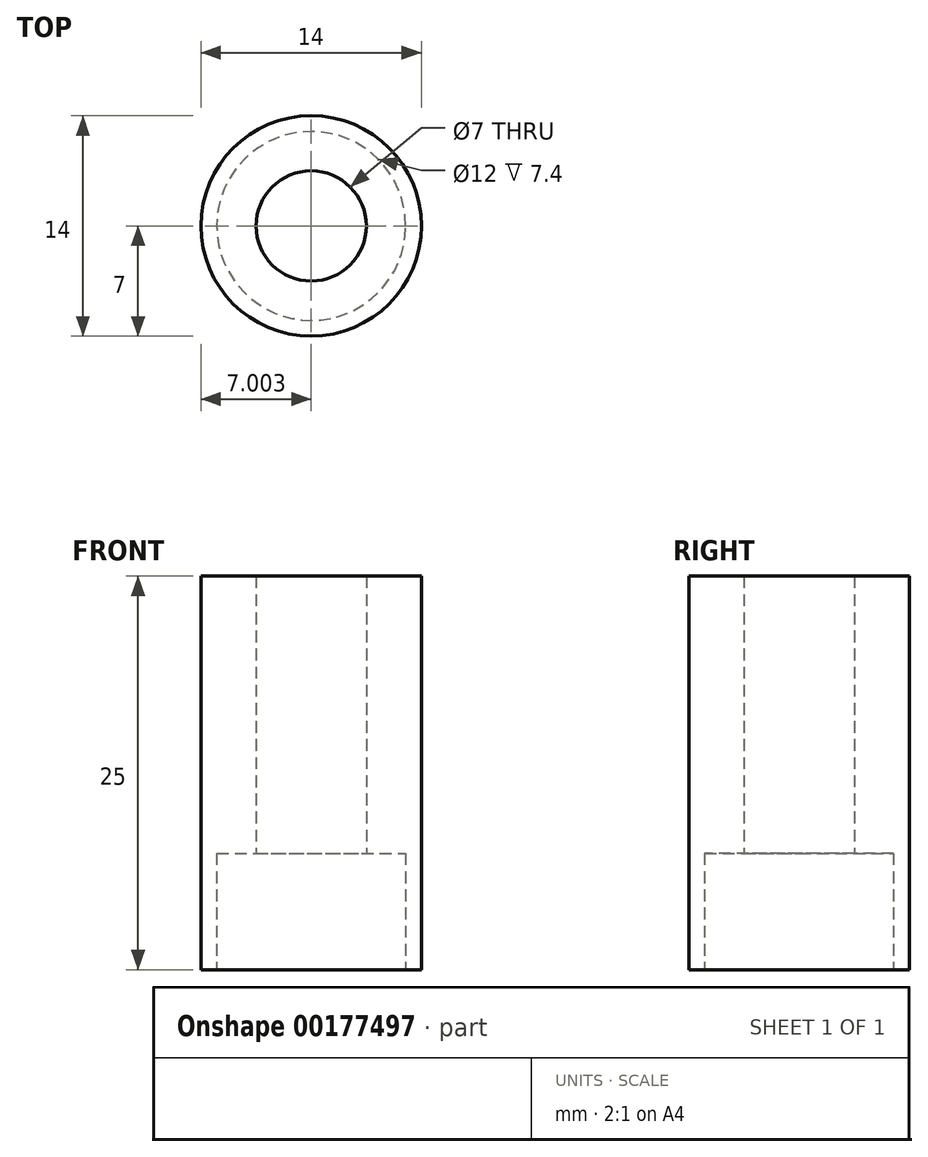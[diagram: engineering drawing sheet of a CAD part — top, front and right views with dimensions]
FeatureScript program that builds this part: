
annotation { "Feature Type Name" : "Feature", "Feature Type Description" : "" }
export const myFeature = defineFeature(function(context is Context, id is Id, definition is map)
    precondition{}
    {
        {
            var Q0;
            Q0=qCreatedBy(makeId("Top.planeOp"),FACE);
            var sketch = newSketch(context, id + "F0", { "sketchPlane" : qUnion([Q0])});
            skCircle(sketch, "E0", {"center": v(1.82, 0) * mm, "radius": 7 * mm});
            skCircle(sketch, "E1", {"center": v(1.82, 0) * mm, "radius": 3.5 * mm});
            skSolve(sketch);
        }
        {
            var Q0;
            Q0=makeQuery(id+"F0.imprint","IMPRINT",FACE,{"disambiguationData":[TD([[makeQuery(id+"F0.imprint","IMPRINT",EDGE,{"derivedFrom":sQuery(id+"F0.wireOp",EDGE,"E0")}),1.0]])]});
            extrude(context, id + "F1", {"entities" : qUnion([Q0]), "depth" : 25 * mm});
        }
        {
            var Q0;
            Q0=makeQuery(id+"F1.opExtrude","CAP_FACE",FACE,{"disambiguationData":[OSD([sQuery(id+"F0.wireOp",EDGE,"E0"),sQuery(id+"F0.wireOp",EDGE,"E1")])],"isStart":true});
            var sketch = newSketch(context, id + "F2", { "sketchPlane" : qUnion([Q0])});
            skCircle(sketch, "E2", {"center": v(1.82, 0) * mm, "radius": 6 * mm});
            skSolve(sketch);
        }
        {
            var Q0;
            Q0 = qSketchRegion(id + "F2", true);
            extrude(context, id + "F3", {"entities" : qUnion([Q0]), "operationType" : NewBodyOperationType.REMOVE, "oppositeDirection" : true, "depth" : 7.4 * mm});
        }
    });
